# Revit family: Zumtobel MIRO NIV LED M625
name_source: partatom
category: Lighting Fixtures
revit_build: Autodesk Revit 2016 (Build: 20150220_1215(x64)
units: mm (PartAtom-declared; Revit-internal decimal feet)

## family parameters
Cut with Voids When Loaded = No
Host = Face
Light Source = Yes
OmniClass Number = 23.80.70.11
OmniClass Title = Luminaries for Internal Lighting
Part Type = Normal
Room Calculation Point = No
Round Connector Dimension = Use Diameter
Shared = No

## types (2) — shared parameters
Assembly Code = D5020200
Color Filter = 16777215
Description = Recessed LED luminaire
Dimming Lamp Color Temperature Shift = <None>
Emit Shape Visible in Rendering = No
Height = 85 mm  [stored 0.278871 ft]
Lamp = LED
Manufacturer = Zumtobel Lighting
Tilt Angle = 90.00°
Voltage = 230 V
zero-valued in all types: Default Elevation

## per-type parameters (varying)
| type | Apparent Load | Emit from Rectangle Length | Emit from Rectangle Width | Length | Model | Photometric Web File | URL | Width |
| MIRO NIV M625L | 28 VA | 310 mm  [stored 1.01706 ft] | 1248 mm  [stored 4.09449 ft] | 1248 mm  [stored 4.09449 ft] | 42928761 | D33416AA_MIRO_NIV_LED3800-840_M625L_EVG.IES | http://www.zumtobel.com | 310 mm  [stored 1.01706 ft] |
| MIRO NIV M625Q | 18 VA | 623 mm  [stored 2.04396 ft] | 623 mm  [stored 2.04396 ft] | 623 mm  [stored 2.04396 ft] | 42182135 | 42182135_(STD_LEO).IES | www.zumtobel.com/42182135 | 623 mm  [stored 2.04396 ft] |

note: [stored X ft] marks values corroborated as IEEE doubles in the binary element streams (Revit-internal decimal feet)

## geometry (parser evidence)
native form markers: Sweep x3
no freeform markers — native parametric forms only
